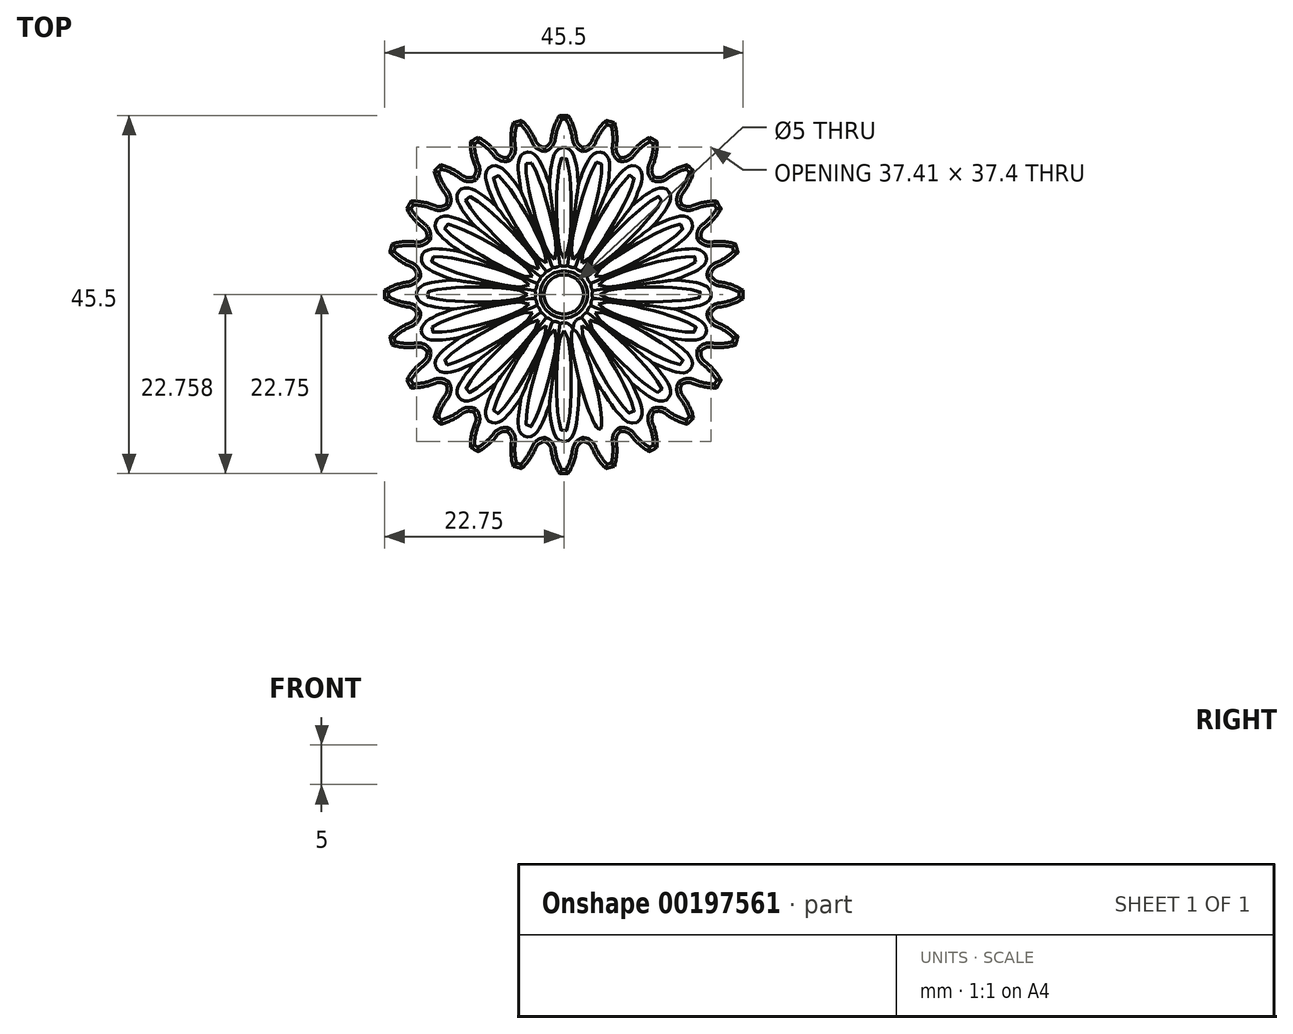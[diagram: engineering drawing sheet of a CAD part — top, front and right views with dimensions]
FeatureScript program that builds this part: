
annotation { "Feature Type Name" : "Feature", "Feature Type Description" : "" }
export const myFeature = defineFeature(function(context is Context, id is Id, definition is map)
    precondition{}
    {
        {
            var Q0;
            Q0=qCreatedBy(makeId("Top.planeOp"),FACE);
            var sketch = newSketch(context, id + "F0", { "sketchPlane" : qUnion([Q0])});
            skCircle(sketch, "E0", {"center": v(0, 0) * mm, "radius": 21 * mm, "construction": true});
            skCircle(sketch, "E1", {"center": v(0, 0) * mm, "radius": 19.74 * mm, "construction": true});
            skLineSegment(sketch, "E2", {"start": v(0, 0) * mm, "end": v(9.48, 32.53) * mm, "construction": true});
            skLineSegment(sketch, "E3", {"start": v(0, 0) * mm, "end": v(-2.71, 41.38) * mm, "construction": true});
            skLineSegment(sketch, "E4", {"start": v(0, 0) * mm, "end": v(0, 51.47) * mm, "construction": true});
            skArc(sketch, "E5", {"start": v(-0.56, 22.74) * mm, "mid": v(-1.24, 21.33) * mm, "end": v(-1.6, 19.8) * mm});
            skArc(sketch, "E6", {"start": v(0, 22.75) * mm, "mid": v(-0.28, 22.75) * mm, "end": v(-0.56, 22.74) * mm});
            skArc(sketch, "E7.MirrorCS", {"start": v(0, 22.75) * mm, "mid": v(0.28, 22.75) * mm, "end": v(0.56, 22.74) * mm});
            skArc(sketch, "E8.MirrorCS", {"start": v(0.56, 22.74) * mm, "mid": v(1.24, 21.33) * mm, "end": v(1.6, 19.8) * mm});
            skArc(sketch, "E9.filletArc", {"start": v(1.6, 19.8) * mm, "mid": v(1.87, 19.12) * mm, "end": v(2.46, 18.69) * mm});
            skArc(sketch, "E10.MirrorCS", {"start": v(-1.6, 19.8) * mm, "mid": v(-1.87, 19.12) * mm, "end": v(-2.46, 18.69) * mm});
            skArc(sketch, "E11.1.0", {"start": v(-6.66, 18.71) * mm, "mid": v(-6.76, 17.99) * mm, "end": v(-7.21, 17.41) * mm});
            skArc(sketch, "E11.1.1", {"start": v(-5.89, 21.97) * mm, "mid": v(-5.62, 22.05) * mm, "end": v(-5.35, 22.11) * mm});
            skArc(sketch, "E11.1.2", {"start": v(-5.89, 21.97) * mm, "mid": v(-6.16, 21.9) * mm, "end": v(-6.42, 21.82) * mm});
            skArc(sketch, "E11.1.3", {"start": v(-5.35, 22.11) * mm, "mid": v(-4.33, 20.92) * mm, "end": v(-3.59, 19.54) * mm});
            skArc(sketch, "E11.1.4", {"start": v(-3.59, 19.54) * mm, "mid": v(-3.14, 18.95) * mm, "end": v(-2.46, 18.69) * mm});
            skArc(sketch, "E11.1.5", {"start": v(-6.42, 21.82) * mm, "mid": v(-6.71, 20.28) * mm, "end": v(-6.66, 18.71) * mm});
            skArc(sketch, "E11.2.0", {"start": v(-11.28, 16.35) * mm, "mid": v(-11.18, 15.62) * mm, "end": v(-11.47, 14.95) * mm});
            skArc(sketch, "E11.2.1", {"start": v(-11.37, 19.7) * mm, "mid": v(-11.13, 19.84) * mm, "end": v(-10.89, 19.97) * mm});
            skArc(sketch, "E11.2.2", {"start": v(-11.38, 19.7) * mm, "mid": v(-11.62, 19.56) * mm, "end": v(-11.85, 19.42) * mm});
            skArc(sketch, "E11.2.3", {"start": v(-10.89, 19.97) * mm, "mid": v(-9.6, 19.09) * mm, "end": v(-8.52, 17.94) * mm});
            skArc(sketch, "E11.2.4", {"start": v(-8.52, 17.94) * mm, "mid": v(-7.94, 17.5) * mm, "end": v(-7.21, 17.41) * mm});
            skArc(sketch, "E11.2.5", {"start": v(-11.85, 19.42) * mm, "mid": v(-11.74, 17.85) * mm, "end": v(-11.28, 16.35) * mm});
            skArc(sketch, "E11.3.0", {"start": v(-15.13, 12.87) * mm, "mid": v(-14.84, 12.2) * mm, "end": v(-14.95, 11.47) * mm});
            skArc(sketch, "E11.3.1", {"start": v(-16.09, 16.09) * mm, "mid": v(-15.89, 16.28) * mm, "end": v(-15.69, 16.48) * mm});
            skArc(sketch, "E11.3.2", {"start": v(-16.09, 16.09) * mm, "mid": v(-16.28, 15.89) * mm, "end": v(-16.48, 15.69) * mm});
            skArc(sketch, "E11.3.3", {"start": v(-15.69, 16.48) * mm, "mid": v(-14.2, 15.96) * mm, "end": v(-12.87, 15.13) * mm});
            skArc(sketch, "E11.3.4", {"start": v(-12.87, 15.13) * mm, "mid": v(-12.2, 14.84) * mm, "end": v(-11.47, 14.95) * mm});
            skArc(sketch, "E11.3.5", {"start": v(-16.48, 15.69) * mm, "mid": v(-15.96, 14.2) * mm, "end": v(-15.13, 12.87) * mm});
            skArc(sketch, "E11.4.0", {"start": v(-17.94, 8.52) * mm, "mid": v(-17.5, 7.94) * mm, "end": v(-17.41, 7.21) * mm});
            skArc(sketch, "E11.4.1", {"start": v(-19.7, 11.38) * mm, "mid": v(-19.56, 11.62) * mm, "end": v(-19.42, 11.85) * mm});
            skArc(sketch, "E11.4.2", {"start": v(-19.7, 11.37) * mm, "mid": v(-19.84, 11.13) * mm, "end": v(-19.97, 10.89) * mm});
            skArc(sketch, "E11.4.3", {"start": v(-19.42, 11.85) * mm, "mid": v(-17.85, 11.74) * mm, "end": v(-16.35, 11.28) * mm});
            skArc(sketch, "E11.4.4", {"start": v(-16.35, 11.28) * mm, "mid": v(-15.62, 11.18) * mm, "end": v(-14.95, 11.47) * mm});
            skArc(sketch, "E11.4.5", {"start": v(-19.97, 10.89) * mm, "mid": v(-19.09, 9.6) * mm, "end": v(-17.94, 8.52) * mm});
            skArc(sketch, "E11.5.0", {"start": v(-19.54, 3.59) * mm, "mid": v(-18.95, 3.14) * mm, "end": v(-18.69, 2.46) * mm});
            skArc(sketch, "E11.5.1", {"start": v(-21.97, 5.89) * mm, "mid": v(-21.9, 6.16) * mm, "end": v(-21.82, 6.42) * mm});
            skArc(sketch, "E11.5.2", {"start": v(-21.97, 5.89) * mm, "mid": v(-22.05, 5.62) * mm, "end": v(-22.11, 5.35) * mm});
            skArc(sketch, "E11.5.3", {"start": v(-21.82, 6.42) * mm, "mid": v(-20.28, 6.71) * mm, "end": v(-18.71, 6.66) * mm});
            skArc(sketch, "E11.5.4", {"start": v(-18.71, 6.66) * mm, "mid": v(-17.99, 6.76) * mm, "end": v(-17.41, 7.21) * mm});
            skArc(sketch, "E11.5.5", {"start": v(-22.11, 5.35) * mm, "mid": v(-20.92, 4.33) * mm, "end": v(-19.54, 3.59) * mm});
            skArc(sketch, "E11.6.0", {"start": v(-19.8, -1.6) * mm, "mid": v(-19.12, -1.87) * mm, "end": v(-18.69, -2.46) * mm});
            skArc(sketch, "E11.6.1", {"start": v(-22.75, 0) * mm, "mid": v(-22.75, 0.28) * mm, "end": v(-22.74, 0.56) * mm});
            skArc(sketch, "E11.6.2", {"start": v(-22.75, 0) * mm, "mid": v(-22.75, -0.28) * mm, "end": v(-22.74, -0.56) * mm});
            skArc(sketch, "E11.6.3", {"start": v(-22.74, 0.56) * mm, "mid": v(-21.33, 1.24) * mm, "end": v(-19.8, 1.6) * mm});
            skArc(sketch, "E11.6.4", {"start": v(-19.8, 1.6) * mm, "mid": v(-19.12, 1.87) * mm, "end": v(-18.69, 2.46) * mm});
            skArc(sketch, "E11.6.5", {"start": v(-22.74, -0.56) * mm, "mid": v(-21.33, -1.24) * mm, "end": v(-19.8, -1.6) * mm});
            skArc(sketch, "E11.7.0", {"start": v(-18.71, -6.66) * mm, "mid": v(-17.99, -6.76) * mm, "end": v(-17.41, -7.21) * mm});
            skArc(sketch, "E11.7.1", {"start": v(-21.97, -5.89) * mm, "mid": v(-22.05, -5.62) * mm, "end": v(-22.11, -5.35) * mm});
            skArc(sketch, "E11.7.2", {"start": v(-21.97, -5.89) * mm, "mid": v(-21.9, -6.16) * mm, "end": v(-21.82, -6.42) * mm});
            skArc(sketch, "E11.7.3", {"start": v(-22.11, -5.35) * mm, "mid": v(-20.92, -4.33) * mm, "end": v(-19.54, -3.59) * mm});
            skArc(sketch, "E11.7.4", {"start": v(-19.54, -3.59) * mm, "mid": v(-18.95, -3.14) * mm, "end": v(-18.69, -2.46) * mm});
            skArc(sketch, "E11.7.5", {"start": v(-21.82, -6.42) * mm, "mid": v(-20.28, -6.71) * mm, "end": v(-18.71, -6.66) * mm});
            skArc(sketch, "E11.8.0", {"start": v(-16.35, -11.28) * mm, "mid": v(-15.62, -11.18) * mm, "end": v(-14.95, -11.47) * mm});
            skArc(sketch, "E11.8.1", {"start": v(-19.7, -11.37) * mm, "mid": v(-19.84, -11.13) * mm, "end": v(-19.97, -10.89) * mm});
            skArc(sketch, "E11.8.2", {"start": v(-19.7, -11.38) * mm, "mid": v(-19.56, -11.62) * mm, "end": v(-19.42, -11.85) * mm});
            skArc(sketch, "E11.8.3", {"start": v(-19.97, -10.89) * mm, "mid": v(-19.09, -9.6) * mm, "end": v(-17.94, -8.52) * mm});
            skArc(sketch, "E11.8.4", {"start": v(-17.94, -8.52) * mm, "mid": v(-17.5, -7.94) * mm, "end": v(-17.41, -7.21) * mm});
            skArc(sketch, "E11.8.5", {"start": v(-19.42, -11.85) * mm, "mid": v(-17.85, -11.74) * mm, "end": v(-16.35, -11.28) * mm});
            skArc(sketch, "E11.9.0", {"start": v(-12.87, -15.13) * mm, "mid": v(-12.2, -14.84) * mm, "end": v(-11.47, -14.95) * mm});
            skArc(sketch, "E11.9.1", {"start": v(-16.09, -16.09) * mm, "mid": v(-16.28, -15.89) * mm, "end": v(-16.48, -15.69) * mm});
            skArc(sketch, "E11.9.2", {"start": v(-16.09, -16.09) * mm, "mid": v(-15.89, -16.28) * mm, "end": v(-15.69, -16.48) * mm});
            skArc(sketch, "E11.9.3", {"start": v(-16.48, -15.69) * mm, "mid": v(-15.96, -14.2) * mm, "end": v(-15.13, -12.87) * mm});
            skArc(sketch, "E11.9.4", {"start": v(-15.13, -12.87) * mm, "mid": v(-14.84, -12.2) * mm, "end": v(-14.95, -11.47) * mm});
            skArc(sketch, "E11.9.5", {"start": v(-15.69, -16.48) * mm, "mid": v(-14.2, -15.96) * mm, "end": v(-12.87, -15.13) * mm});
            skArc(sketch, "E11.10.0", {"start": v(-8.52, -17.94) * mm, "mid": v(-7.94, -17.5) * mm, "end": v(-7.21, -17.41) * mm});
            skArc(sketch, "E11.10.1", {"start": v(-11.38, -19.7) * mm, "mid": v(-11.62, -19.56) * mm, "end": v(-11.85, -19.42) * mm});
            skArc(sketch, "E11.10.2", {"start": v(-11.37, -19.7) * mm, "mid": v(-11.13, -19.84) * mm, "end": v(-10.89, -19.97) * mm});
            skArc(sketch, "E11.10.3", {"start": v(-11.85, -19.42) * mm, "mid": v(-11.74, -17.85) * mm, "end": v(-11.28, -16.35) * mm});
            skArc(sketch, "E11.10.4", {"start": v(-11.28, -16.35) * mm, "mid": v(-11.18, -15.62) * mm, "end": v(-11.47, -14.95) * mm});
            skArc(sketch, "E11.10.5", {"start": v(-10.89, -19.97) * mm, "mid": v(-9.6, -19.09) * mm, "end": v(-8.52, -17.94) * mm});
            skArc(sketch, "E11.11.0", {"start": v(-3.59, -19.54) * mm, "mid": v(-3.14, -18.95) * mm, "end": v(-2.46, -18.69) * mm});
            skArc(sketch, "E11.11.1", {"start": v(-5.89, -21.97) * mm, "mid": v(-6.16, -21.9) * mm, "end": v(-6.42, -21.82) * mm});
            skArc(sketch, "E11.11.2", {"start": v(-5.89, -21.97) * mm, "mid": v(-5.62, -22.05) * mm, "end": v(-5.35, -22.11) * mm});
            skArc(sketch, "E11.11.3", {"start": v(-6.42, -21.82) * mm, "mid": v(-6.71, -20.28) * mm, "end": v(-6.66, -18.71) * mm});
            skArc(sketch, "E11.11.4", {"start": v(-6.66, -18.71) * mm, "mid": v(-6.76, -17.99) * mm, "end": v(-7.21, -17.41) * mm});
            skArc(sketch, "E11.11.5", {"start": v(-5.35, -22.11) * mm, "mid": v(-4.33, -20.92) * mm, "end": v(-3.59, -19.54) * mm});
            skArc(sketch, "E11.12.0", {"start": v(1.6, -19.8) * mm, "mid": v(1.87, -19.12) * mm, "end": v(2.46, -18.69) * mm});
            skArc(sketch, "E11.12.1", {"start": v(0, -22.75) * mm, "mid": v(-0.28, -22.75) * mm, "end": v(-0.56, -22.74) * mm});
            skArc(sketch, "E11.12.2", {"start": v(0, -22.75) * mm, "mid": v(0.28, -22.75) * mm, "end": v(0.56, -22.74) * mm});
            skArc(sketch, "E11.12.3", {"start": v(-0.56, -22.74) * mm, "mid": v(-1.24, -21.33) * mm, "end": v(-1.6, -19.8) * mm});
            skArc(sketch, "E11.12.4", {"start": v(-1.6, -19.8) * mm, "mid": v(-1.87, -19.12) * mm, "end": v(-2.46, -18.69) * mm});
            skArc(sketch, "E11.12.5", {"start": v(0.56, -22.74) * mm, "mid": v(1.24, -21.33) * mm, "end": v(1.6, -19.8) * mm});
            skArc(sketch, "E11.13.0", {"start": v(6.66, -18.71) * mm, "mid": v(6.76, -17.99) * mm, "end": v(7.21, -17.41) * mm});
            skArc(sketch, "E11.13.1", {"start": v(5.89, -21.97) * mm, "mid": v(5.62, -22.05) * mm, "end": v(5.35, -22.11) * mm});
            skArc(sketch, "E11.13.2", {"start": v(5.89, -21.97) * mm, "mid": v(6.16, -21.9) * mm, "end": v(6.42, -21.82) * mm});
            skArc(sketch, "E11.13.3", {"start": v(5.35, -22.11) * mm, "mid": v(4.33, -20.92) * mm, "end": v(3.59, -19.54) * mm});
            skArc(sketch, "E11.13.4", {"start": v(3.59, -19.54) * mm, "mid": v(3.14, -18.95) * mm, "end": v(2.46, -18.69) * mm});
            skArc(sketch, "E11.13.5", {"start": v(6.42, -21.82) * mm, "mid": v(6.71, -20.28) * mm, "end": v(6.66, -18.71) * mm});
            skArc(sketch, "E11.14.0", {"start": v(11.28, -16.35) * mm, "mid": v(11.18, -15.62) * mm, "end": v(11.47, -14.95) * mm});
            skArc(sketch, "E11.14.1", {"start": v(11.37, -19.7) * mm, "mid": v(11.13, -19.84) * mm, "end": v(10.89, -19.97) * mm});
            skArc(sketch, "E11.14.2", {"start": v(11.37, -19.7) * mm, "mid": v(11.62, -19.56) * mm, "end": v(11.85, -19.42) * mm});
            skArc(sketch, "E11.14.3", {"start": v(10.89, -19.97) * mm, "mid": v(9.6, -19.09) * mm, "end": v(8.52, -17.94) * mm});
            skArc(sketch, "E11.14.4", {"start": v(8.52, -17.94) * mm, "mid": v(7.94, -17.5) * mm, "end": v(7.21, -17.41) * mm});
            skArc(sketch, "E11.14.5", {"start": v(11.85, -19.42) * mm, "mid": v(11.74, -17.85) * mm, "end": v(11.28, -16.35) * mm});
            skArc(sketch, "E11.15.0", {"start": v(15.13, -12.87) * mm, "mid": v(14.84, -12.2) * mm, "end": v(14.95, -11.47) * mm});
            skArc(sketch, "E11.15.1", {"start": v(16.09, -16.09) * mm, "mid": v(15.89, -16.28) * mm, "end": v(15.69, -16.48) * mm});
            skArc(sketch, "E11.15.2", {"start": v(16.09, -16.09) * mm, "mid": v(16.28, -15.89) * mm, "end": v(16.48, -15.69) * mm});
            skArc(sketch, "E11.15.3", {"start": v(15.69, -16.48) * mm, "mid": v(14.2, -15.96) * mm, "end": v(12.87, -15.13) * mm});
            skArc(sketch, "E11.15.4", {"start": v(12.87, -15.13) * mm, "mid": v(12.2, -14.84) * mm, "end": v(11.47, -14.95) * mm});
            skArc(sketch, "E11.15.5", {"start": v(16.48, -15.69) * mm, "mid": v(15.96, -14.2) * mm, "end": v(15.13, -12.87) * mm});
            skArc(sketch, "E11.16.0", {"start": v(17.94, -8.52) * mm, "mid": v(17.5, -7.94) * mm, "end": v(17.41, -7.21) * mm});
            skArc(sketch, "E11.16.1", {"start": v(19.7, -11.38) * mm, "mid": v(19.56, -11.62) * mm, "end": v(19.42, -11.85) * mm});
            skArc(sketch, "E11.16.2", {"start": v(19.7, -11.38) * mm, "mid": v(19.84, -11.13) * mm, "end": v(19.97, -10.89) * mm});
            skArc(sketch, "E11.16.3", {"start": v(19.42, -11.85) * mm, "mid": v(17.85, -11.74) * mm, "end": v(16.35, -11.28) * mm});
            skArc(sketch, "E11.16.4", {"start": v(16.35, -11.28) * mm, "mid": v(15.62, -11.18) * mm, "end": v(14.95, -11.47) * mm});
            skArc(sketch, "E11.16.5", {"start": v(19.97, -10.89) * mm, "mid": v(19.09, -9.6) * mm, "end": v(17.94, -8.52) * mm});
            skArc(sketch, "E11.17.0", {"start": v(19.54, -3.59) * mm, "mid": v(18.95, -3.14) * mm, "end": v(18.69, -2.46) * mm});
            skArc(sketch, "E11.17.1", {"start": v(21.97, -5.89) * mm, "mid": v(21.9, -6.16) * mm, "end": v(21.82, -6.42) * mm});
            skArc(sketch, "E11.17.2", {"start": v(21.97, -5.89) * mm, "mid": v(22.05, -5.62) * mm, "end": v(22.11, -5.35) * mm});
            skArc(sketch, "E11.17.3", {"start": v(21.82, -6.42) * mm, "mid": v(20.28, -6.71) * mm, "end": v(18.71, -6.66) * mm});
            skArc(sketch, "E11.17.4", {"start": v(18.71, -6.66) * mm, "mid": v(17.99, -6.76) * mm, "end": v(17.41, -7.21) * mm});
            skArc(sketch, "E11.17.5", {"start": v(22.11, -5.35) * mm, "mid": v(20.92, -4.33) * mm, "end": v(19.54, -3.59) * mm});
            skArc(sketch, "E11.18.0", {"start": v(19.8, 1.6) * mm, "mid": v(19.12, 1.87) * mm, "end": v(18.69, 2.46) * mm});
            skArc(sketch, "E11.18.1", {"start": v(22.75, 0) * mm, "mid": v(22.75, -0.28) * mm, "end": v(22.74, -0.56) * mm});
            skArc(sketch, "E11.18.2", {"start": v(22.75, 0) * mm, "mid": v(22.75, 0.28) * mm, "end": v(22.74, 0.56) * mm});
            skArc(sketch, "E11.18.3", {"start": v(22.74, -0.56) * mm, "mid": v(21.33, -1.24) * mm, "end": v(19.8, -1.6) * mm});
            skArc(sketch, "E11.18.4", {"start": v(19.8, -1.6) * mm, "mid": v(19.12, -1.87) * mm, "end": v(18.69, -2.46) * mm});
            skArc(sketch, "E11.18.5", {"start": v(22.74, 0.56) * mm, "mid": v(21.33, 1.24) * mm, "end": v(19.8, 1.6) * mm});
            skArc(sketch, "E11.19.0", {"start": v(18.71, 6.66) * mm, "mid": v(17.99, 6.76) * mm, "end": v(17.41, 7.21) * mm});
            skArc(sketch, "E11.19.1", {"start": v(21.97, 5.89) * mm, "mid": v(22.05, 5.62) * mm, "end": v(22.11, 5.35) * mm});
            skArc(sketch, "E11.19.2", {"start": v(21.97, 5.89) * mm, "mid": v(21.9, 6.16) * mm, "end": v(21.82, 6.42) * mm});
            skArc(sketch, "E11.19.3", {"start": v(22.11, 5.35) * mm, "mid": v(20.92, 4.33) * mm, "end": v(19.54, 3.59) * mm});
            skArc(sketch, "E11.19.4", {"start": v(19.54, 3.59) * mm, "mid": v(18.95, 3.14) * mm, "end": v(18.69, 2.46) * mm});
            skArc(sketch, "E11.19.5", {"start": v(21.82, 6.42) * mm, "mid": v(20.28, 6.71) * mm, "end": v(18.71, 6.66) * mm});
            skArc(sketch, "E11.20.0", {"start": v(16.35, 11.28) * mm, "mid": v(15.62, 11.18) * mm, "end": v(14.95, 11.47) * mm});
            skArc(sketch, "E11.20.1", {"start": v(19.7, 11.37) * mm, "mid": v(19.84, 11.13) * mm, "end": v(19.97, 10.89) * mm});
            skArc(sketch, "E11.20.2", {"start": v(19.7, 11.38) * mm, "mid": v(19.56, 11.62) * mm, "end": v(19.42, 11.85) * mm});
            skArc(sketch, "E11.20.3", {"start": v(19.97, 10.89) * mm, "mid": v(19.09, 9.6) * mm, "end": v(17.94, 8.52) * mm});
            skArc(sketch, "E11.20.4", {"start": v(17.94, 8.52) * mm, "mid": v(17.5, 7.94) * mm, "end": v(17.41, 7.21) * mm});
            skArc(sketch, "E11.20.5", {"start": v(19.42, 11.85) * mm, "mid": v(17.85, 11.74) * mm, "end": v(16.35, 11.28) * mm});
            skArc(sketch, "E11.21.0", {"start": v(12.87, 15.13) * mm, "mid": v(12.2, 14.84) * mm, "end": v(11.47, 14.95) * mm});
            skArc(sketch, "E11.21.1", {"start": v(16.09, 16.09) * mm, "mid": v(16.28, 15.89) * mm, "end": v(16.48, 15.69) * mm});
            skArc(sketch, "E11.21.2", {"start": v(16.09, 16.09) * mm, "mid": v(15.89, 16.28) * mm, "end": v(15.69, 16.48) * mm});
            skArc(sketch, "E11.21.3", {"start": v(16.48, 15.69) * mm, "mid": v(15.96, 14.2) * mm, "end": v(15.13, 12.87) * mm});
            skArc(sketch, "E11.21.4", {"start": v(15.13, 12.87) * mm, "mid": v(14.84, 12.2) * mm, "end": v(14.95, 11.47) * mm});
            skArc(sketch, "E11.21.5", {"start": v(15.69, 16.48) * mm, "mid": v(14.2, 15.96) * mm, "end": v(12.87, 15.13) * mm});
            skArc(sketch, "E11.22.0", {"start": v(8.52, 17.94) * mm, "mid": v(7.94, 17.5) * mm, "end": v(7.21, 17.41) * mm});
            skArc(sketch, "E11.22.1", {"start": v(11.38, 19.7) * mm, "mid": v(11.62, 19.56) * mm, "end": v(11.85, 19.42) * mm});
            skArc(sketch, "E11.22.2", {"start": v(11.38, 19.7) * mm, "mid": v(11.13, 19.84) * mm, "end": v(10.89, 19.97) * mm});
            skArc(sketch, "E11.22.3", {"start": v(11.85, 19.42) * mm, "mid": v(11.74, 17.85) * mm, "end": v(11.28, 16.35) * mm});
            skArc(sketch, "E11.22.4", {"start": v(11.28, 16.35) * mm, "mid": v(11.18, 15.62) * mm, "end": v(11.47, 14.95) * mm});
            skArc(sketch, "E11.22.5", {"start": v(10.89, 19.97) * mm, "mid": v(9.6, 19.09) * mm, "end": v(8.52, 17.94) * mm});
            skArc(sketch, "E11.23.0", {"start": v(3.59, 19.54) * mm, "mid": v(3.14, 18.95) * mm, "end": v(2.46, 18.69) * mm});
            skArc(sketch, "E11.23.1", {"start": v(5.89, 21.97) * mm, "mid": v(6.16, 21.9) * mm, "end": v(6.42, 21.82) * mm});
            skArc(sketch, "E11.23.2", {"start": v(5.89, 21.97) * mm, "mid": v(5.62, 22.05) * mm, "end": v(5.35, 22.11) * mm});
            skArc(sketch, "E11.23.3", {"start": v(6.42, 21.82) * mm, "mid": v(6.71, 20.28) * mm, "end": v(6.66, 18.71) * mm});
            skArc(sketch, "E11.23.4", {"start": v(6.66, 18.71) * mm, "mid": v(6.76, 17.99) * mm, "end": v(7.21, 17.41) * mm});
            skArc(sketch, "E11.23.5", {"start": v(5.35, 22.11) * mm, "mid": v(4.33, 20.92) * mm, "end": v(3.59, 19.54) * mm});
            skCircle(sketch, "E12", {"center": v(0, 0) * mm, "radius": 2.5 * mm});
            skLineSegment(sketch, "E13", {"start": v(-5.35, 22.11) * mm, "end": v(-0.56, 22.74) * mm, "construction": true});
            skSolve(sketch);
        }
        {
            var Q0;
            Q0=makeQuery(id+"F0.imprint","IMPRINT",FACE,{"disambiguationData":[TD([[makeQuery(id+"F0.imprint","IMPRINT",EDGE,{"derivedFrom":sQuery(id+"F0.wireOp",EDGE,"E5")}),1.0]])]});
            extrude(context, id + "F1", {"entities" : qUnion([Q0]), "depth" : 5 * mm});
        }
        {
            var Q0;
            Q0=makeQuery(id+"F1.opExtrude","CAP_FACE",FACE,{"disambiguationData":[OSD([sQuery(id+"F0.wireOp",EDGE,"E5"),sQuery(id+"F0.wireOp",EDGE,"E6"),sQuery(id+"F0.wireOp",EDGE,"E7.MirrorCS"),sQuery(id+"F0.wireOp",EDGE,"E8.MirrorCS"),sQuery(id+"F0.wireOp",EDGE,"E9.filletArc"),sQuery(id+"F0.wireOp",EDGE,"E10.MirrorCS"),sQuery(id+"F0.wireOp",EDGE,"E11.1.0"),sQuery(id+"F0.wireOp",EDGE,"E11.1.1"),sQuery(id+"F0.wireOp",EDGE,"E11.1.2"),sQuery(id+"F0.wireOp",EDGE,"E11.1.3"),sQuery(id+"F0.wireOp",EDGE,"E11.1.4"),sQuery(id+"F0.wireOp",EDGE,"E11.1.5"),sQuery(id+"F0.wireOp",EDGE,"E11.2.0"),sQuery(id+"F0.wireOp",EDGE,"E11.2.1"),sQuery(id+"F0.wireOp",EDGE,"E11.2.2"),sQuery(id+"F0.wireOp",EDGE,"E11.2.3"),sQuery(id+"F0.wireOp",EDGE,"E11.2.4"),sQuery(id+"F0.wireOp",EDGE,"E11.2.5"),sQuery(id+"F0.wireOp",EDGE,"E11.3.0"),sQuery(id+"F0.wireOp",EDGE,"E11.3.1"),sQuery(id+"F0.wireOp",EDGE,"E11.3.2"),sQuery(id+"F0.wireOp",EDGE,"E11.3.3"),sQuery(id+"F0.wireOp",EDGE,"E11.3.4"),sQuery(id+"F0.wireOp",EDGE,"E11.3.5"),sQuery(id+"F0.wireOp",EDGE,"E11.4.0"),sQuery(id+"F0.wireOp",EDGE,"E11.4.1"),sQuery(id+"F0.wireOp",EDGE,"E11.4.2"),sQuery(id+"F0.wireOp",EDGE,"E11.4.3"),sQuery(id+"F0.wireOp",EDGE,"E11.4.4"),sQuery(id+"F0.wireOp",EDGE,"E11.4.5"),sQuery(id+"F0.wireOp",EDGE,"E11.5.0"),sQuery(id+"F0.wireOp",EDGE,"E11.5.1"),sQuery(id+"F0.wireOp",EDGE,"E11.5.2"),sQuery(id+"F0.wireOp",EDGE,"E11.5.3"),sQuery(id+"F0.wireOp",EDGE,"E11.5.4"),sQuery(id+"F0.wireOp",EDGE,"E11.5.5"),sQuery(id+"F0.wireOp",EDGE,"E11.6.0"),sQuery(id+"F0.wireOp",EDGE,"E11.6.1"),sQuery(id+"F0.wireOp",EDGE,"E11.6.2"),sQuery(id+"F0.wireOp",EDGE,"E11.6.3"),sQuery(id+"F0.wireOp",EDGE,"E11.6.4"),sQuery(id+"F0.wireOp",EDGE,"E11.6.5"),sQuery(id+"F0.wireOp",EDGE,"E11.7.0"),sQuery(id+"F0.wireOp",EDGE,"E11.7.1"),sQuery(id+"F0.wireOp",EDGE,"E11.7.2"),sQuery(id+"F0.wireOp",EDGE,"E11.7.3"),sQuery(id+"F0.wireOp",EDGE,"E11.7.4"),sQuery(id+"F0.wireOp",EDGE,"E11.7.5"),sQuery(id+"F0.wireOp",EDGE,"E11.8.0"),sQuery(id+"F0.wireOp",EDGE,"E11.8.1"),sQuery(id+"F0.wireOp",EDGE,"E11.8.2"),sQuery(id+"F0.wireOp",EDGE,"E11.8.3"),sQuery(id+"F0.wireOp",EDGE,"E11.8.4"),sQuery(id+"F0.wireOp",EDGE,"E11.8.5"),sQuery(id+"F0.wireOp",EDGE,"E11.9.0"),sQuery(id+"F0.wireOp",EDGE,"E11.9.1"),sQuery(id+"F0.wireOp",EDGE,"E11.9.2"),sQuery(id+"F0.wireOp",EDGE,"E11.9.3"),sQuery(id+"F0.wireOp",EDGE,"E11.9.4"),sQuery(id+"F0.wireOp",EDGE,"E11.9.5"),sQuery(id+"F0.wireOp",EDGE,"E11.10.0"),sQuery(id+"F0.wireOp",EDGE,"E11.10.1"),sQuery(id+"F0.wireOp",EDGE,"E11.10.2"),sQuery(id+"F0.wireOp",EDGE,"E11.10.3"),sQuery(id+"F0.wireOp",EDGE,"E11.10.4"),sQuery(id+"F0.wireOp",EDGE,"E11.10.5"),sQuery(id+"F0.wireOp",EDGE,"E11.11.0"),sQuery(id+"F0.wireOp",EDGE,"E11.11.1"),sQuery(id+"F0.wireOp",EDGE,"E11.11.2"),sQuery(id+"F0.wireOp",EDGE,"E11.11.3"),sQuery(id+"F0.wireOp",EDGE,"E11.11.4"),sQuery(id+"F0.wireOp",EDGE,"E11.11.5"),sQuery(id+"F0.wireOp",EDGE,"E11.12.0"),sQuery(id+"F0.wireOp",EDGE,"E11.12.1"),sQuery(id+"F0.wireOp",EDGE,"E11.12.2"),sQuery(id+"F0.wireOp",EDGE,"E11.12.3"),sQuery(id+"F0.wireOp",EDGE,"E11.12.4"),sQuery(id+"F0.wireOp",EDGE,"E11.12.5"),sQuery(id+"F0.wireOp",EDGE,"E11.13.0"),sQuery(id+"F0.wireOp",EDGE,"E11.13.1"),sQuery(id+"F0.wireOp",EDGE,"E11.13.2"),sQuery(id+"F0.wireOp",EDGE,"E11.13.3"),sQuery(id+"F0.wireOp",EDGE,"E11.13.4"),sQuery(id+"F0.wireOp",EDGE,"E11.13.5"),sQuery(id+"F0.wireOp",EDGE,"E11.14.0"),sQuery(id+"F0.wireOp",EDGE,"E11.14.1"),sQuery(id+"F0.wireOp",EDGE,"E11.14.2"),sQuery(id+"F0.wireOp",EDGE,"E11.14.3"),sQuery(id+"F0.wireOp",EDGE,"E11.14.4"),sQuery(id+"F0.wireOp",EDGE,"E11.14.5"),sQuery(id+"F0.wireOp",EDGE,"E11.15.0"),sQuery(id+"F0.wireOp",EDGE,"E11.15.1"),sQuery(id+"F0.wireOp",EDGE,"E11.15.2"),sQuery(id+"F0.wireOp",EDGE,"E11.15.3"),sQuery(id+"F0.wireOp",EDGE,"E11.15.4"),sQuery(id+"F0.wireOp",EDGE,"E11.15.5"),sQuery(id+"F0.wireOp",EDGE,"E11.16.0"),sQuery(id+"F0.wireOp",EDGE,"E11.16.1"),sQuery(id+"F0.wireOp",EDGE,"E11.16.2"),sQuery(id+"F0.wireOp",EDGE,"E11.16.3"),sQuery(id+"F0.wireOp",EDGE,"E11.16.4"),sQuery(id+"F0.wireOp",EDGE,"E11.16.5"),sQuery(id+"F0.wireOp",EDGE,"E11.17.0"),sQuery(id+"F0.wireOp",EDGE,"E11.17.1"),sQuery(id+"F0.wireOp",EDGE,"E11.17.2"),sQuery(id+"F0.wireOp",EDGE,"E11.17.3"),sQuery(id+"F0.wireOp",EDGE,"E11.17.4"),sQuery(id+"F0.wireOp",EDGE,"E11.17.5"),sQuery(id+"F0.wireOp",EDGE,"E11.18.0"),sQuery(id+"F0.wireOp",EDGE,"E11.18.1"),sQuery(id+"F0.wireOp",EDGE,"E11.18.2"),sQuery(id+"F0.wireOp",EDGE,"E11.18.3"),sQuery(id+"F0.wireOp",EDGE,"E11.18.4"),sQuery(id+"F0.wireOp",EDGE,"E11.18.5"),sQuery(id+"F0.wireOp",EDGE,"E11.19.0"),sQuery(id+"F0.wireOp",EDGE,"E11.19.1"),sQuery(id+"F0.wireOp",EDGE,"E11.19.2"),sQuery(id+"F0.wireOp",EDGE,"E11.19.3"),sQuery(id+"F0.wireOp",EDGE,"E11.19.4"),sQuery(id+"F0.wireOp",EDGE,"E11.19.5"),sQuery(id+"F0.wireOp",EDGE,"E11.20.0"),sQuery(id+"F0.wireOp",EDGE,"E11.20.1"),sQuery(id+"F0.wireOp",EDGE,"E11.20.2"),sQuery(id+"F0.wireOp",EDGE,"E11.20.3"),sQuery(id+"F0.wireOp",EDGE,"E11.20.4"),sQuery(id+"F0.wireOp",EDGE,"E11.20.5"),sQuery(id+"F0.wireOp",EDGE,"E11.21.0"),sQuery(id+"F0.wireOp",EDGE,"E11.21.1"),sQuery(id+"F0.wireOp",EDGE,"E11.21.2"),sQuery(id+"F0.wireOp",EDGE,"E11.21.3"),sQuery(id+"F0.wireOp",EDGE,"E11.21.4"),sQuery(id+"F0.wireOp",EDGE,"E11.21.5"),sQuery(id+"F0.wireOp",EDGE,"E11.22.0"),sQuery(id+"F0.wireOp",EDGE,"E11.22.1"),sQuery(id+"F0.wireOp",EDGE,"E11.22.2"),sQuery(id+"F0.wireOp",EDGE,"E11.22.3"),sQuery(id+"F0.wireOp",EDGE,"E11.22.4"),sQuery(id+"F0.wireOp",EDGE,"E11.22.5"),sQuery(id+"F0.wireOp",EDGE,"E11.23.0"),sQuery(id+"F0.wireOp",EDGE,"E11.23.1"),sQuery(id+"F0.wireOp",EDGE,"E11.23.2"),sQuery(id+"F0.wireOp",EDGE,"E11.23.3"),sQuery(id+"F0.wireOp",EDGE,"E11.23.4"),sQuery(id+"F0.wireOp",EDGE,"E11.23.5"),sQuery(id+"F0.wireOp",EDGE,"E12")])],"isStart":false});
            var Q1;
            Q1=makeQuery(id+"F1.opExtrude","CAP_FACE",FACE,{"disambiguationData":[OSD([sQuery(id+"F0.wireOp",EDGE,"E5"),sQuery(id+"F0.wireOp",EDGE,"E6"),sQuery(id+"F0.wireOp",EDGE,"E7.MirrorCS"),sQuery(id+"F0.wireOp",EDGE,"E8.MirrorCS"),sQuery(id+"F0.wireOp",EDGE,"E9.filletArc"),sQuery(id+"F0.wireOp",EDGE,"E10.MirrorCS"),sQuery(id+"F0.wireOp",EDGE,"E11.1.0"),sQuery(id+"F0.wireOp",EDGE,"E11.1.1"),sQuery(id+"F0.wireOp",EDGE,"E11.1.2"),sQuery(id+"F0.wireOp",EDGE,"E11.1.3"),sQuery(id+"F0.wireOp",EDGE,"E11.1.4"),sQuery(id+"F0.wireOp",EDGE,"E11.1.5"),sQuery(id+"F0.wireOp",EDGE,"E11.2.0"),sQuery(id+"F0.wireOp",EDGE,"E11.2.1"),sQuery(id+"F0.wireOp",EDGE,"E11.2.2"),sQuery(id+"F0.wireOp",EDGE,"E11.2.3"),sQuery(id+"F0.wireOp",EDGE,"E11.2.4"),sQuery(id+"F0.wireOp",EDGE,"E11.2.5"),sQuery(id+"F0.wireOp",EDGE,"E11.3.0"),sQuery(id+"F0.wireOp",EDGE,"E11.3.1"),sQuery(id+"F0.wireOp",EDGE,"E11.3.2"),sQuery(id+"F0.wireOp",EDGE,"E11.3.3"),sQuery(id+"F0.wireOp",EDGE,"E11.3.4"),sQuery(id+"F0.wireOp",EDGE,"E11.3.5"),sQuery(id+"F0.wireOp",EDGE,"E11.4.0"),sQuery(id+"F0.wireOp",EDGE,"E11.4.1"),sQuery(id+"F0.wireOp",EDGE,"E11.4.2"),sQuery(id+"F0.wireOp",EDGE,"E11.4.3"),sQuery(id+"F0.wireOp",EDGE,"E11.4.4"),sQuery(id+"F0.wireOp",EDGE,"E11.4.5"),sQuery(id+"F0.wireOp",EDGE,"E11.5.0"),sQuery(id+"F0.wireOp",EDGE,"E11.5.1"),sQuery(id+"F0.wireOp",EDGE,"E11.5.2"),sQuery(id+"F0.wireOp",EDGE,"E11.5.3"),sQuery(id+"F0.wireOp",EDGE,"E11.5.4"),sQuery(id+"F0.wireOp",EDGE,"E11.5.5"),sQuery(id+"F0.wireOp",EDGE,"E11.6.0"),sQuery(id+"F0.wireOp",EDGE,"E11.6.1"),sQuery(id+"F0.wireOp",EDGE,"E11.6.2"),sQuery(id+"F0.wireOp",EDGE,"E11.6.3"),sQuery(id+"F0.wireOp",EDGE,"E11.6.4"),sQuery(id+"F0.wireOp",EDGE,"E11.6.5"),sQuery(id+"F0.wireOp",EDGE,"E11.7.0"),sQuery(id+"F0.wireOp",EDGE,"E11.7.1"),sQuery(id+"F0.wireOp",EDGE,"E11.7.2"),sQuery(id+"F0.wireOp",EDGE,"E11.7.3"),sQuery(id+"F0.wireOp",EDGE,"E11.7.4"),sQuery(id+"F0.wireOp",EDGE,"E11.7.5"),sQuery(id+"F0.wireOp",EDGE,"E11.8.0"),sQuery(id+"F0.wireOp",EDGE,"E11.8.1"),sQuery(id+"F0.wireOp",EDGE,"E11.8.2"),sQuery(id+"F0.wireOp",EDGE,"E11.8.3"),sQuery(id+"F0.wireOp",EDGE,"E11.8.4"),sQuery(id+"F0.wireOp",EDGE,"E11.8.5"),sQuery(id+"F0.wireOp",EDGE,"E11.9.0"),sQuery(id+"F0.wireOp",EDGE,"E11.9.1"),sQuery(id+"F0.wireOp",EDGE,"E11.9.2"),sQuery(id+"F0.wireOp",EDGE,"E11.9.3"),sQuery(id+"F0.wireOp",EDGE,"E11.9.4"),sQuery(id+"F0.wireOp",EDGE,"E11.9.5"),sQuery(id+"F0.wireOp",EDGE,"E11.10.0"),sQuery(id+"F0.wireOp",EDGE,"E11.10.1"),sQuery(id+"F0.wireOp",EDGE,"E11.10.2"),sQuery(id+"F0.wireOp",EDGE,"E11.10.3"),sQuery(id+"F0.wireOp",EDGE,"E11.10.4"),sQuery(id+"F0.wireOp",EDGE,"E11.10.5"),sQuery(id+"F0.wireOp",EDGE,"E11.11.0"),sQuery(id+"F0.wireOp",EDGE,"E11.11.1"),sQuery(id+"F0.wireOp",EDGE,"E11.11.2"),sQuery(id+"F0.wireOp",EDGE,"E11.11.3"),sQuery(id+"F0.wireOp",EDGE,"E11.11.4"),sQuery(id+"F0.wireOp",EDGE,"E11.11.5"),sQuery(id+"F0.wireOp",EDGE,"E11.12.0"),sQuery(id+"F0.wireOp",EDGE,"E11.12.1"),sQuery(id+"F0.wireOp",EDGE,"E11.12.2"),sQuery(id+"F0.wireOp",EDGE,"E11.12.3"),sQuery(id+"F0.wireOp",EDGE,"E11.12.4"),sQuery(id+"F0.wireOp",EDGE,"E11.12.5"),sQuery(id+"F0.wireOp",EDGE,"E11.13.0"),sQuery(id+"F0.wireOp",EDGE,"E11.13.1"),sQuery(id+"F0.wireOp",EDGE,"E11.13.2"),sQuery(id+"F0.wireOp",EDGE,"E11.13.3"),sQuery(id+"F0.wireOp",EDGE,"E11.13.4"),sQuery(id+"F0.wireOp",EDGE,"E11.13.5"),sQuery(id+"F0.wireOp",EDGE,"E11.14.0"),sQuery(id+"F0.wireOp",EDGE,"E11.14.1"),sQuery(id+"F0.wireOp",EDGE,"E11.14.2"),sQuery(id+"F0.wireOp",EDGE,"E11.14.3"),sQuery(id+"F0.wireOp",EDGE,"E11.14.4"),sQuery(id+"F0.wireOp",EDGE,"E11.14.5"),sQuery(id+"F0.wireOp",EDGE,"E11.15.0"),sQuery(id+"F0.wireOp",EDGE,"E11.15.1"),sQuery(id+"F0.wireOp",EDGE,"E11.15.2"),sQuery(id+"F0.wireOp",EDGE,"E11.15.3"),sQuery(id+"F0.wireOp",EDGE,"E11.15.4"),sQuery(id+"F0.wireOp",EDGE,"E11.15.5"),sQuery(id+"F0.wireOp",EDGE,"E11.16.0"),sQuery(id+"F0.wireOp",EDGE,"E11.16.1"),sQuery(id+"F0.wireOp",EDGE,"E11.16.2"),sQuery(id+"F0.wireOp",EDGE,"E11.16.3"),sQuery(id+"F0.wireOp",EDGE,"E11.16.4"),sQuery(id+"F0.wireOp",EDGE,"E11.16.5"),sQuery(id+"F0.wireOp",EDGE,"E11.17.0"),sQuery(id+"F0.wireOp",EDGE,"E11.17.1"),sQuery(id+"F0.wireOp",EDGE,"E11.17.2"),sQuery(id+"F0.wireOp",EDGE,"E11.17.3"),sQuery(id+"F0.wireOp",EDGE,"E11.17.4"),sQuery(id+"F0.wireOp",EDGE,"E11.17.5"),sQuery(id+"F0.wireOp",EDGE,"E11.18.0"),sQuery(id+"F0.wireOp",EDGE,"E11.18.1"),sQuery(id+"F0.wireOp",EDGE,"E11.18.2"),sQuery(id+"F0.wireOp",EDGE,"E11.18.3"),sQuery(id+"F0.wireOp",EDGE,"E11.18.4"),sQuery(id+"F0.wireOp",EDGE,"E11.18.5"),sQuery(id+"F0.wireOp",EDGE,"E11.19.0"),sQuery(id+"F0.wireOp",EDGE,"E11.19.1"),sQuery(id+"F0.wireOp",EDGE,"E11.19.2"),sQuery(id+"F0.wireOp",EDGE,"E11.19.3"),sQuery(id+"F0.wireOp",EDGE,"E11.19.4"),sQuery(id+"F0.wireOp",EDGE,"E11.19.5"),sQuery(id+"F0.wireOp",EDGE,"E11.20.0"),sQuery(id+"F0.wireOp",EDGE,"E11.20.1"),sQuery(id+"F0.wireOp",EDGE,"E11.20.2"),sQuery(id+"F0.wireOp",EDGE,"E11.20.3"),sQuery(id+"F0.wireOp",EDGE,"E11.20.4"),sQuery(id+"F0.wireOp",EDGE,"E11.20.5"),sQuery(id+"F0.wireOp",EDGE,"E11.21.0"),sQuery(id+"F0.wireOp",EDGE,"E11.21.1"),sQuery(id+"F0.wireOp",EDGE,"E11.21.2"),sQuery(id+"F0.wireOp",EDGE,"E11.21.3"),sQuery(id+"F0.wireOp",EDGE,"E11.21.4"),sQuery(id+"F0.wireOp",EDGE,"E11.21.5"),sQuery(id+"F0.wireOp",EDGE,"E11.22.0"),sQuery(id+"F0.wireOp",EDGE,"E11.22.1"),sQuery(id+"F0.wireOp",EDGE,"E11.22.2"),sQuery(id+"F0.wireOp",EDGE,"E11.22.3"),sQuery(id+"F0.wireOp",EDGE,"E11.22.4"),sQuery(id+"F0.wireOp",EDGE,"E11.22.5"),sQuery(id+"F0.wireOp",EDGE,"E11.23.0"),sQuery(id+"F0.wireOp",EDGE,"E11.23.1"),sQuery(id+"F0.wireOp",EDGE,"E11.23.2"),sQuery(id+"F0.wireOp",EDGE,"E11.23.3"),sQuery(id+"F0.wireOp",EDGE,"E11.23.4"),sQuery(id+"F0.wireOp",EDGE,"E11.23.5"),sQuery(id+"F0.wireOp",EDGE,"E12")])],"isStart":true});
            chamfer(context, id + "F2", {"entities" : qUnion([Q0, Q1]), "width" : .5 * mm, "tangentPropagation" : true});
        }
        {
            var Q0;
            Q0=makeQuery(id+"F1.opExtrude","CAP_FACE",FACE,{"disambiguationData":[OSD([sQuery(id+"F0.wireOp",EDGE,"E5"),sQuery(id+"F0.wireOp",EDGE,"E6"),sQuery(id+"F0.wireOp",EDGE,"E7.MirrorCS"),sQuery(id+"F0.wireOp",EDGE,"E8.MirrorCS"),sQuery(id+"F0.wireOp",EDGE,"E9.filletArc"),sQuery(id+"F0.wireOp",EDGE,"E10.MirrorCS"),sQuery(id+"F0.wireOp",EDGE,"E11.1.0"),sQuery(id+"F0.wireOp",EDGE,"E11.1.1"),sQuery(id+"F0.wireOp",EDGE,"E11.1.2"),sQuery(id+"F0.wireOp",EDGE,"E11.1.3"),sQuery(id+"F0.wireOp",EDGE,"E11.1.4"),sQuery(id+"F0.wireOp",EDGE,"E11.1.5"),sQuery(id+"F0.wireOp",EDGE,"E11.2.0"),sQuery(id+"F0.wireOp",EDGE,"E11.2.1"),sQuery(id+"F0.wireOp",EDGE,"E11.2.2"),sQuery(id+"F0.wireOp",EDGE,"E11.2.3"),sQuery(id+"F0.wireOp",EDGE,"E11.2.4"),sQuery(id+"F0.wireOp",EDGE,"E11.2.5"),sQuery(id+"F0.wireOp",EDGE,"E11.3.0"),sQuery(id+"F0.wireOp",EDGE,"E11.3.1"),sQuery(id+"F0.wireOp",EDGE,"E11.3.2"),sQuery(id+"F0.wireOp",EDGE,"E11.3.3"),sQuery(id+"F0.wireOp",EDGE,"E11.3.4"),sQuery(id+"F0.wireOp",EDGE,"E11.3.5"),sQuery(id+"F0.wireOp",EDGE,"E11.4.0"),sQuery(id+"F0.wireOp",EDGE,"E11.4.1"),sQuery(id+"F0.wireOp",EDGE,"E11.4.2"),sQuery(id+"F0.wireOp",EDGE,"E11.4.3"),sQuery(id+"F0.wireOp",EDGE,"E11.4.4"),sQuery(id+"F0.wireOp",EDGE,"E11.4.5"),sQuery(id+"F0.wireOp",EDGE,"E11.5.0"),sQuery(id+"F0.wireOp",EDGE,"E11.5.1"),sQuery(id+"F0.wireOp",EDGE,"E11.5.2"),sQuery(id+"F0.wireOp",EDGE,"E11.5.3"),sQuery(id+"F0.wireOp",EDGE,"E11.5.4"),sQuery(id+"F0.wireOp",EDGE,"E11.5.5"),sQuery(id+"F0.wireOp",EDGE,"E11.6.0"),sQuery(id+"F0.wireOp",EDGE,"E11.6.1"),sQuery(id+"F0.wireOp",EDGE,"E11.6.2"),sQuery(id+"F0.wireOp",EDGE,"E11.6.3"),sQuery(id+"F0.wireOp",EDGE,"E11.6.4"),sQuery(id+"F0.wireOp",EDGE,"E11.6.5"),sQuery(id+"F0.wireOp",EDGE,"E11.7.0"),sQuery(id+"F0.wireOp",EDGE,"E11.7.1"),sQuery(id+"F0.wireOp",EDGE,"E11.7.2"),sQuery(id+"F0.wireOp",EDGE,"E11.7.3"),sQuery(id+"F0.wireOp",EDGE,"E11.7.4"),sQuery(id+"F0.wireOp",EDGE,"E11.7.5"),sQuery(id+"F0.wireOp",EDGE,"E11.8.0"),sQuery(id+"F0.wireOp",EDGE,"E11.8.1"),sQuery(id+"F0.wireOp",EDGE,"E11.8.2"),sQuery(id+"F0.wireOp",EDGE,"E11.8.3"),sQuery(id+"F0.wireOp",EDGE,"E11.8.4"),sQuery(id+"F0.wireOp",EDGE,"E11.8.5"),sQuery(id+"F0.wireOp",EDGE,"E11.9.0"),sQuery(id+"F0.wireOp",EDGE,"E11.9.1"),sQuery(id+"F0.wireOp",EDGE,"E11.9.2"),sQuery(id+"F0.wireOp",EDGE,"E11.9.3"),sQuery(id+"F0.wireOp",EDGE,"E11.9.4"),sQuery(id+"F0.wireOp",EDGE,"E11.9.5"),sQuery(id+"F0.wireOp",EDGE,"E11.10.0"),sQuery(id+"F0.wireOp",EDGE,"E11.10.1"),sQuery(id+"F0.wireOp",EDGE,"E11.10.2"),sQuery(id+"F0.wireOp",EDGE,"E11.10.3"),sQuery(id+"F0.wireOp",EDGE,"E11.10.4"),sQuery(id+"F0.wireOp",EDGE,"E11.10.5"),sQuery(id+"F0.wireOp",EDGE,"E11.11.0"),sQuery(id+"F0.wireOp",EDGE,"E11.11.1"),sQuery(id+"F0.wireOp",EDGE,"E11.11.2"),sQuery(id+"F0.wireOp",EDGE,"E11.11.3"),sQuery(id+"F0.wireOp",EDGE,"E11.11.4"),sQuery(id+"F0.wireOp",EDGE,"E11.11.5"),sQuery(id+"F0.wireOp",EDGE,"E11.12.0"),sQuery(id+"F0.wireOp",EDGE,"E11.12.1"),sQuery(id+"F0.wireOp",EDGE,"E11.12.2"),sQuery(id+"F0.wireOp",EDGE,"E11.12.3"),sQuery(id+"F0.wireOp",EDGE,"E11.12.4"),sQuery(id+"F0.wireOp",EDGE,"E11.12.5"),sQuery(id+"F0.wireOp",EDGE,"E11.13.0"),sQuery(id+"F0.wireOp",EDGE,"E11.13.1"),sQuery(id+"F0.wireOp",EDGE,"E11.13.2"),sQuery(id+"F0.wireOp",EDGE,"E11.13.3"),sQuery(id+"F0.wireOp",EDGE,"E11.13.4"),sQuery(id+"F0.wireOp",EDGE,"E11.13.5"),sQuery(id+"F0.wireOp",EDGE,"E11.14.0"),sQuery(id+"F0.wireOp",EDGE,"E11.14.1"),sQuery(id+"F0.wireOp",EDGE,"E11.14.2"),sQuery(id+"F0.wireOp",EDGE,"E11.14.3"),sQuery(id+"F0.wireOp",EDGE,"E11.14.4"),sQuery(id+"F0.wireOp",EDGE,"E11.14.5"),sQuery(id+"F0.wireOp",EDGE,"E11.15.0"),sQuery(id+"F0.wireOp",EDGE,"E11.15.1"),sQuery(id+"F0.wireOp",EDGE,"E11.15.2"),sQuery(id+"F0.wireOp",EDGE,"E11.15.3"),sQuery(id+"F0.wireOp",EDGE,"E11.15.4"),sQuery(id+"F0.wireOp",EDGE,"E11.15.5"),sQuery(id+"F0.wireOp",EDGE,"E11.16.0"),sQuery(id+"F0.wireOp",EDGE,"E11.16.1"),sQuery(id+"F0.wireOp",EDGE,"E11.16.2"),sQuery(id+"F0.wireOp",EDGE,"E11.16.3"),sQuery(id+"F0.wireOp",EDGE,"E11.16.4"),sQuery(id+"F0.wireOp",EDGE,"E11.16.5"),sQuery(id+"F0.wireOp",EDGE,"E11.17.0"),sQuery(id+"F0.wireOp",EDGE,"E11.17.1"),sQuery(id+"F0.wireOp",EDGE,"E11.17.2"),sQuery(id+"F0.wireOp",EDGE,"E11.17.3"),sQuery(id+"F0.wireOp",EDGE,"E11.17.4"),sQuery(id+"F0.wireOp",EDGE,"E11.17.5"),sQuery(id+"F0.wireOp",EDGE,"E11.18.0"),sQuery(id+"F0.wireOp",EDGE,"E11.18.1"),sQuery(id+"F0.wireOp",EDGE,"E11.18.2"),sQuery(id+"F0.wireOp",EDGE,"E11.18.3"),sQuery(id+"F0.wireOp",EDGE,"E11.18.4"),sQuery(id+"F0.wireOp",EDGE,"E11.18.5"),sQuery(id+"F0.wireOp",EDGE,"E11.19.0"),sQuery(id+"F0.wireOp",EDGE,"E11.19.1"),sQuery(id+"F0.wireOp",EDGE,"E11.19.2"),sQuery(id+"F0.wireOp",EDGE,"E11.19.3"),sQuery(id+"F0.wireOp",EDGE,"E11.19.4"),sQuery(id+"F0.wireOp",EDGE,"E11.19.5"),sQuery(id+"F0.wireOp",EDGE,"E11.20.0"),sQuery(id+"F0.wireOp",EDGE,"E11.20.1"),sQuery(id+"F0.wireOp",EDGE,"E11.20.2"),sQuery(id+"F0.wireOp",EDGE,"E11.20.3"),sQuery(id+"F0.wireOp",EDGE,"E11.20.4"),sQuery(id+"F0.wireOp",EDGE,"E11.20.5"),sQuery(id+"F0.wireOp",EDGE,"E11.21.0"),sQuery(id+"F0.wireOp",EDGE,"E11.21.1"),sQuery(id+"F0.wireOp",EDGE,"E11.21.2"),sQuery(id+"F0.wireOp",EDGE,"E11.21.3"),sQuery(id+"F0.wireOp",EDGE,"E11.21.4"),sQuery(id+"F0.wireOp",EDGE,"E11.21.5"),sQuery(id+"F0.wireOp",EDGE,"E11.22.0"),sQuery(id+"F0.wireOp",EDGE,"E11.22.1"),sQuery(id+"F0.wireOp",EDGE,"E11.22.2"),sQuery(id+"F0.wireOp",EDGE,"E11.22.3"),sQuery(id+"F0.wireOp",EDGE,"E11.22.4"),sQuery(id+"F0.wireOp",EDGE,"E11.22.5"),sQuery(id+"F0.wireOp",EDGE,"E11.23.0"),sQuery(id+"F0.wireOp",EDGE,"E11.23.1"),sQuery(id+"F0.wireOp",EDGE,"E11.23.2"),sQuery(id+"F0.wireOp",EDGE,"E11.23.3"),sQuery(id+"F0.wireOp",EDGE,"E11.23.4"),sQuery(id+"F0.wireOp",EDGE,"E11.23.5"),sQuery(id+"F0.wireOp",EDGE,"E12")])],"isStart":false});
            var sketch = newSketch(context, id + "F3", { "sketchPlane" : qUnion([Q0])});
            skEllipse(sketch, "E14", {"center": v(0, 11.14) * mm, "majorRadius": 6.56 * mm, "minorRadius": 0.94 * mm, "majorAxis": v(0, -1)});
            skEllipse(sketch, "E15.1.0", {"center": v(-2.88, 10.77) * mm, "majorRadius": 6.56 * mm, "minorRadius": 0.94 * mm, "majorAxis": v(0.26, -0.97)});
            skEllipse(sketch, "E15.2.0", {"center": v(-5.57, 9.65) * mm, "majorRadius": 6.56 * mm, "minorRadius": 0.94 * mm, "majorAxis": v(0.5, -0.87)});
            skEllipse(sketch, "E15.3.0", {"center": v(-7.88, 7.88) * mm, "majorRadius": 6.56 * mm, "minorRadius": 0.94 * mm, "majorAxis": v(0.7, -0.7)});
            skEllipse(sketch, "E15.4.0", {"center": v(-9.65, 5.57) * mm, "majorRadius": 6.56 * mm, "minorRadius": 0.94 * mm, "majorAxis": v(0.87, -0.5)});
            skEllipse(sketch, "E15.5.0", {"center": v(-10.77, 2.88) * mm, "majorRadius": 6.56 * mm, "minorRadius": 0.94 * mm, "majorAxis": v(0.97, -0.26)});
            skEllipse(sketch, "E15.6.0", {"center": v(-11.14, 0) * mm, "majorRadius": 6.56 * mm, "minorRadius": 0.94 * mm, "majorAxis": v(1, 0)});
            skEllipse(sketch, "E15.7.0", {"center": v(-10.77, -2.88) * mm, "majorRadius": 6.56 * mm, "minorRadius": 0.94 * mm, "majorAxis": v(0.97, 0.26)});
            skEllipse(sketch, "E15.8.0", {"center": v(-9.65, -5.57) * mm, "majorRadius": 6.56 * mm, "minorRadius": 0.94 * mm, "majorAxis": v(0.87, 0.5)});
            skEllipse(sketch, "E15.9.0", {"center": v(-7.88, -7.88) * mm, "majorRadius": 6.56 * mm, "minorRadius": 0.94 * mm, "majorAxis": v(0.7, 0.7)});
            skEllipse(sketch, "E15.10.0", {"center": v(-5.57, -9.65) * mm, "majorRadius": 6.56 * mm, "minorRadius": 0.94 * mm, "majorAxis": v(0.5, 0.87)});
            skEllipse(sketch, "E15.11.0", {"center": v(-2.88, -10.77) * mm, "majorRadius": 6.56 * mm, "minorRadius": 0.94 * mm, "majorAxis": v(0.26, 0.97)});
            skEllipse(sketch, "E15.12.0", {"center": v(0, -11.14) * mm, "majorRadius": 6.56 * mm, "minorRadius": 0.94 * mm, "majorAxis": v(0, 1)});
            skEllipse(sketch, "E15.13.0", {"center": v(2.88, -10.77) * mm, "majorRadius": 6.56 * mm, "minorRadius": 0.94 * mm, "majorAxis": v(-0.26, 0.97)});
            skEllipse(sketch, "E15.14.0", {"center": v(5.57, -9.65) * mm, "majorRadius": 6.56 * mm, "minorRadius": 0.94 * mm, "majorAxis": v(-0.5, 0.87)});
            skEllipse(sketch, "E15.15.0", {"center": v(7.88, -7.88) * mm, "majorRadius": 6.56 * mm, "minorRadius": 0.94 * mm, "majorAxis": v(-0.7, 0.7)});
            skEllipse(sketch, "E15.16.0", {"center": v(9.65, -5.57) * mm, "majorRadius": 6.56 * mm, "minorRadius": 0.94 * mm, "majorAxis": v(-0.87, 0.5)});
            skEllipse(sketch, "E15.17.0", {"center": v(10.77, -2.88) * mm, "majorRadius": 6.56 * mm, "minorRadius": 0.94 * mm, "majorAxis": v(-0.97, 0.26)});
            skEllipse(sketch, "E15.18.0", {"center": v(11.14, 0) * mm, "majorRadius": 6.56 * mm, "minorRadius": 0.94 * mm, "majorAxis": v(-1, 0)});
            skEllipse(sketch, "E15.19.0", {"center": v(10.77, 2.88) * mm, "majorRadius": 6.56 * mm, "minorRadius": 0.94 * mm, "majorAxis": v(-0.97, -0.26)});
            skEllipse(sketch, "E15.20.0", {"center": v(9.65, 5.57) * mm, "majorRadius": 6.56 * mm, "minorRadius": 0.94 * mm, "majorAxis": v(-0.87, -0.5)});
            skEllipse(sketch, "E15.21.0", {"center": v(7.88, 7.88) * mm, "majorRadius": 6.56 * mm, "minorRadius": 0.94 * mm, "majorAxis": v(-0.7, -0.7)});
            skEllipse(sketch, "E15.22.0", {"center": v(5.57, 9.65) * mm, "majorRadius": 6.56 * mm, "minorRadius": 0.94 * mm, "majorAxis": v(-0.5, -0.87)});
            skEllipse(sketch, "E15.23.0", {"center": v(2.88, 10.77) * mm, "majorRadius": 6.56 * mm, "minorRadius": 0.94 * mm, "majorAxis": v(-0.26, -0.97)});
            skPoint(sketch, "E15.center", {"position": v(0, 0) * mm});
            skSolve(sketch);
        }
        {
            var Q0;
            Q0=makeQuery(id+"F3.imprint","IMPRINT",FACE,{"disambiguationData":[TD([[makeQuery(id+"F3.imprint","IMPRINT",EDGE,{"derivedFrom":sQuery(id+"F3.wireOp",EDGE,"E15.8.0")}),1.0]])]});
            var Q1;
            Q1=makeQuery(id+"F3.imprint","IMPRINT",FACE,{"disambiguationData":[TD([[makeQuery(id+"F3.imprint","IMPRINT",EDGE,{"derivedFrom":sQuery(id+"F3.wireOp",EDGE,"E15.9.0")}),1.0]])]});
            var Q2;
            Q2=makeQuery(id+"F3.imprint","IMPRINT",FACE,{"disambiguationData":[TD([[makeQuery(id+"F3.imprint","IMPRINT",EDGE,{"derivedFrom":sQuery(id+"F3.wireOp",EDGE,"E15.10.0")}),1.0]])]});
            var Q3;
            Q3=makeQuery(id+"F3.imprint","IMPRINT",FACE,{"disambiguationData":[TD([[makeQuery(id+"F3.imprint","IMPRINT",EDGE,{"derivedFrom":sQuery(id+"F3.wireOp",EDGE,"E15.11.0")}),1.0]])]});
            var Q4;
            Q4=makeQuery(id+"F3.imprint","IMPRINT",FACE,{"disambiguationData":[TD([[makeQuery(id+"F3.imprint","IMPRINT",EDGE,{"derivedFrom":sQuery(id+"F3.wireOp",EDGE,"E15.12.0")}),1.0]])]});
            var Q5;
            Q5=makeQuery(id+"F3.imprint","IMPRINT",FACE,{"disambiguationData":[TD([[makeQuery(id+"F3.imprint","IMPRINT",EDGE,{"derivedFrom":sQuery(id+"F3.wireOp",EDGE,"E15.13.0")}),1.0]])]});
            var Q6;
            Q6=makeQuery(id+"F3.imprint","IMPRINT",FACE,{"disambiguationData":[TD([[makeQuery(id+"F3.imprint","IMPRINT",EDGE,{"derivedFrom":sQuery(id+"F3.wireOp",EDGE,"E15.14.0")}),1.0]])]});
            var Q7;
            Q7=makeQuery(id+"F3.imprint","IMPRINT",FACE,{"disambiguationData":[TD([[makeQuery(id+"F3.imprint","IMPRINT",EDGE,{"derivedFrom":sQuery(id+"F3.wireOp",EDGE,"E15.15.0")}),1.0]])]});
            var Q8;
            Q8=makeQuery(id+"F3.imprint","IMPRINT",FACE,{"disambiguationData":[TD([[makeQuery(id+"F3.imprint","IMPRINT",EDGE,{"derivedFrom":sQuery(id+"F3.wireOp",EDGE,"E15.16.0")}),1.0]])]});
            var Q9;
            Q9=makeQuery(id+"F3.imprint","IMPRINT",FACE,{"disambiguationData":[TD([[makeQuery(id+"F3.imprint","IMPRINT",EDGE,{"derivedFrom":sQuery(id+"F3.wireOp",EDGE,"E15.17.0")}),1.0]])]});
            var Q10;
            Q10=makeQuery(id+"F3.imprint","IMPRINT",FACE,{"disambiguationData":[TD([[makeQuery(id+"F3.imprint","IMPRINT",EDGE,{"derivedFrom":sQuery(id+"F3.wireOp",EDGE,"E15.18.0")}),1.0]])]});
            var Q11;
            Q11=makeQuery(id+"F3.imprint","IMPRINT",FACE,{"disambiguationData":[TD([[makeQuery(id+"F3.imprint","IMPRINT",EDGE,{"derivedFrom":sQuery(id+"F3.wireOp",EDGE,"E15.19.0")}),1.0]])]});
            var Q12;
            Q12=makeQuery(id+"F3.imprint","IMPRINT",FACE,{"disambiguationData":[TD([[makeQuery(id+"F3.imprint","IMPRINT",EDGE,{"derivedFrom":sQuery(id+"F3.wireOp",EDGE,"E15.20.0")}),1.0]])]});
            var Q13;
            Q13=makeQuery(id+"F3.imprint","IMPRINT",FACE,{"disambiguationData":[TD([[makeQuery(id+"F3.imprint","IMPRINT",EDGE,{"derivedFrom":sQuery(id+"F3.wireOp",EDGE,"E15.21.0")}),1.0]])]});
            var Q14;
            Q14=makeQuery(id+"F3.imprint","IMPRINT",FACE,{"disambiguationData":[TD([[makeQuery(id+"F3.imprint","IMPRINT",EDGE,{"derivedFrom":sQuery(id+"F3.wireOp",EDGE,"E15.22.0")}),1.0]])]});
            var Q15;
            Q15=makeQuery(id+"F3.imprint","IMPRINT",FACE,{"disambiguationData":[TD([[makeQuery(id+"F3.imprint","IMPRINT",EDGE,{"derivedFrom":sQuery(id+"F3.wireOp",EDGE,"E15.23.0")}),1.0]])]});
            var Q16;
            Q16=makeQuery(id+"F3.imprint","IMPRINT",FACE,{"disambiguationData":[TD([[makeQuery(id+"F3.imprint","IMPRINT",EDGE,{"derivedFrom":sQuery(id+"F3.wireOp",EDGE,"E14")}),1.0]])]});
            var Q17;
            Q17=makeQuery(id+"F3.imprint","IMPRINT",FACE,{"disambiguationData":[TD([[makeQuery(id+"F3.imprint","IMPRINT",EDGE,{"derivedFrom":sQuery(id+"F3.wireOp",EDGE,"E15.1.0")}),1.0]])]});
            var Q18;
            Q18=makeQuery(id+"F3.imprint","IMPRINT",FACE,{"disambiguationData":[TD([[makeQuery(id+"F3.imprint","IMPRINT",EDGE,{"derivedFrom":sQuery(id+"F3.wireOp",EDGE,"E15.2.0")}),1.0]])]});
            var Q19;
            Q19=makeQuery(id+"F3.imprint","IMPRINT",FACE,{"disambiguationData":[TD([[makeQuery(id+"F3.imprint","IMPRINT",EDGE,{"derivedFrom":sQuery(id+"F3.wireOp",EDGE,"E15.3.0")}),1.0]])]});
            var Q20;
            Q20=makeQuery(id+"F3.imprint","IMPRINT",FACE,{"disambiguationData":[TD([[makeQuery(id+"F3.imprint","IMPRINT",EDGE,{"derivedFrom":sQuery(id+"F3.wireOp",EDGE,"E15.4.0")}),1.0]])]});
            var Q21;
            Q21=makeQuery(id+"F3.imprint","IMPRINT",FACE,{"disambiguationData":[TD([[makeQuery(id+"F3.imprint","IMPRINT",EDGE,{"derivedFrom":sQuery(id+"F3.wireOp",EDGE,"E15.5.0")}),1.0]])]});
            var Q22;
            Q22=makeQuery(id+"F3.imprint","IMPRINT",FACE,{"disambiguationData":[TD([[makeQuery(id+"F3.imprint","IMPRINT",EDGE,{"derivedFrom":sQuery(id+"F3.wireOp",EDGE,"E15.6.0")}),1.0]])]});
            var Q23;
            Q23=makeQuery(id+"F3.imprint","IMPRINT",FACE,{"disambiguationData":[TD([[makeQuery(id+"F3.imprint","IMPRINT",EDGE,{"derivedFrom":sQuery(id+"F3.wireOp",EDGE,"E15.7.0")}),1.0]])]});
            extrude(context, id + "F4", {"entities" : qUnion([Q0, Q1, Q2, Q3, Q4, Q5, Q6, Q7, Q8, Q9, Q10, Q11, Q12, Q13, Q14, Q15, Q16, Q17, Q18, Q19, Q20, Q21, Q22, Q23]), "operationType" : NewBodyOperationType.REMOVE, "endBound" : BoundingType.UP_TO_NEXT, "oppositeDirection" : true, "depth" : 25 * mm});
        }
        {
            var Q0;
            Q0=makeQuery(id+"F4.boolean.opBoolean","COPY",FACE,{"derivedFrom":makeQuery(id+"F4.opExtrude","SWEPT_FACE",FACE,{"disambiguationData":[OSD([sQuery(id+"F3.wireOp",EDGE,"E15.22.0")])]})});
            var Q1;
            Q1=makeQuery(id+"F4.boolean.opBoolean","COPY",FACE,{"derivedFrom":makeQuery(id+"F4.opExtrude","SWEPT_FACE",FACE,{"disambiguationData":[OSD([sQuery(id+"F3.wireOp",EDGE,"E15.23.0")])]})});
            var Q2;
            Q2=makeQuery(id+"F4.boolean.opBoolean","COPY",FACE,{"derivedFrom":makeQuery(id+"F4.opExtrude","SWEPT_FACE",FACE,{"disambiguationData":[OSD([sQuery(id+"F3.wireOp",EDGE,"E15.21.0")])]})});
            var Q3;
            Q3=makeQuery(id+"F4.boolean.opBoolean","COPY",FACE,{"derivedFrom":makeQuery(id+"F4.opExtrude","SWEPT_FACE",FACE,{"disambiguationData":[OSD([sQuery(id+"F3.wireOp",EDGE,"E15.20.0")])]})});
            var Q4;
            Q4=makeQuery(id+"F4.boolean.opBoolean","COPY",FACE,{"derivedFrom":makeQuery(id+"F4.opExtrude","SWEPT_FACE",FACE,{"disambiguationData":[OSD([sQuery(id+"F3.wireOp",EDGE,"E15.19.0")])]})});
            var Q5;
            Q5=makeQuery(id+"F4.boolean.opBoolean","COPY",FACE,{"derivedFrom":makeQuery(id+"F4.opExtrude","SWEPT_FACE",FACE,{"disambiguationData":[OSD([sQuery(id+"F3.wireOp",EDGE,"E15.18.0")])]})});
            var Q6;
            Q6=makeQuery(id+"F4.boolean.opBoolean","COPY",FACE,{"derivedFrom":makeQuery(id+"F4.opExtrude","SWEPT_FACE",FACE,{"disambiguationData":[OSD([sQuery(id+"F3.wireOp",EDGE,"E15.17.0")])]})});
            var Q7;
            Q7=makeQuery(id+"F4.boolean.opBoolean","COPY",FACE,{"derivedFrom":makeQuery(id+"F4.opExtrude","SWEPT_FACE",FACE,{"disambiguationData":[OSD([sQuery(id+"F3.wireOp",EDGE,"E15.16.0")])]})});
            var Q8;
            Q8=makeQuery(id+"F4.boolean.opBoolean","COPY",FACE,{"derivedFrom":makeQuery(id+"F4.opExtrude","SWEPT_FACE",FACE,{"disambiguationData":[OSD([sQuery(id+"F3.wireOp",EDGE,"E15.15.0")])]})});
            var Q9;
            Q9=makeQuery(id+"F4.boolean.opBoolean","COPY",FACE,{"derivedFrom":makeQuery(id+"F4.opExtrude","SWEPT_FACE",FACE,{"disambiguationData":[OSD([sQuery(id+"F3.wireOp",EDGE,"E15.14.0")])]})});
            var Q10;
            Q10=makeQuery(id+"F4.boolean.opBoolean","COPY",FACE,{"derivedFrom":makeQuery(id+"F4.opExtrude","SWEPT_FACE",FACE,{"disambiguationData":[OSD([sQuery(id+"F3.wireOp",EDGE,"E14")])]})});
            var Q11;
            Q11=makeQuery(id+"F4.boolean.opBoolean","COPY",FACE,{"derivedFrom":makeQuery(id+"F4.opExtrude","SWEPT_FACE",FACE,{"disambiguationData":[OSD([sQuery(id+"F3.wireOp",EDGE,"E15.1.0")])]})});
            var Q12;
            Q12=makeQuery(id+"F4.boolean.opBoolean","COPY",FACE,{"derivedFrom":makeQuery(id+"F4.opExtrude","SWEPT_FACE",FACE,{"disambiguationData":[OSD([sQuery(id+"F3.wireOp",EDGE,"E15.3.0")])]})});
            var Q13;
            Q13=makeQuery(id+"F4.boolean.opBoolean","COPY",FACE,{"derivedFrom":makeQuery(id+"F4.opExtrude","SWEPT_FACE",FACE,{"disambiguationData":[OSD([sQuery(id+"F3.wireOp",EDGE,"E15.4.0")])]})});
            var Q14;
            Q14=makeQuery(id+"F4.boolean.opBoolean","COPY",FACE,{"derivedFrom":makeQuery(id+"F4.opExtrude","SWEPT_FACE",FACE,{"disambiguationData":[OSD([sQuery(id+"F3.wireOp",EDGE,"E15.5.0")])]})});
            var Q15;
            Q15=makeQuery(id+"F4.boolean.opBoolean","COPY",FACE,{"derivedFrom":makeQuery(id+"F4.opExtrude","SWEPT_FACE",FACE,{"disambiguationData":[OSD([sQuery(id+"F3.wireOp",EDGE,"E15.2.0")])]})});
            var Q16;
            Q16=makeQuery(id+"F4.boolean.opBoolean","COPY",FACE,{"derivedFrom":makeQuery(id+"F4.opExtrude","SWEPT_FACE",FACE,{"disambiguationData":[OSD([sQuery(id+"F3.wireOp",EDGE,"E15.6.0")])]})});
            var Q17;
            Q17=makeQuery(id+"F4.boolean.opBoolean","COPY",FACE,{"derivedFrom":makeQuery(id+"F4.opExtrude","SWEPT_FACE",FACE,{"disambiguationData":[OSD([sQuery(id+"F3.wireOp",EDGE,"E15.7.0")])]})});
            var Q18;
            Q18=makeQuery(id+"F4.boolean.opBoolean","COPY",FACE,{"derivedFrom":makeQuery(id+"F4.opExtrude","SWEPT_FACE",FACE,{"disambiguationData":[OSD([sQuery(id+"F3.wireOp",EDGE,"E15.8.0")])]})});
            var Q19;
            Q19=makeQuery(id+"F4.boolean.opBoolean","COPY",FACE,{"derivedFrom":makeQuery(id+"F4.opExtrude","SWEPT_FACE",FACE,{"disambiguationData":[OSD([sQuery(id+"F3.wireOp",EDGE,"E15.9.0")])]})});
            var Q20;
            Q20=makeQuery(id+"F4.boolean.opBoolean","COPY",FACE,{"derivedFrom":makeQuery(id+"F4.opExtrude","SWEPT_FACE",FACE,{"disambiguationData":[OSD([sQuery(id+"F3.wireOp",EDGE,"E15.10.0")])]})});
            var Q21;
            Q21=makeQuery(id+"F4.boolean.opBoolean","COPY",FACE,{"derivedFrom":makeQuery(id+"F4.opExtrude","SWEPT_FACE",FACE,{"disambiguationData":[OSD([sQuery(id+"F3.wireOp",EDGE,"E15.11.0")])]})});
            var Q22;
            Q22=makeQuery(id+"F4.boolean.opBoolean","COPY",FACE,{"derivedFrom":makeQuery(id+"F4.opExtrude","SWEPT_FACE",FACE,{"disambiguationData":[OSD([sQuery(id+"F3.wireOp",EDGE,"E15.12.0")])]})});
            fillet(context, id + "F5", {"entities" : qUnion([Q0, Q1, Q2, Q3, Q4, Q5, Q6, Q7, Q8, Q9, Q10, Q11, Q12, Q13, Q14, Q15, Q16, Q17, Q18, Q19, Q20, Q21, Q22]), "radius" : 1 * mm, "tangentPropagation" : true, "allowEdgeOverflow" : false});
        }
    });
